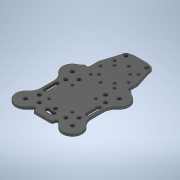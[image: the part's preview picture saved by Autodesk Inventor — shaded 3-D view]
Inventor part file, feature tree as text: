
AUTODESK INVENTOR PART (.ipt)
format: ipt  version: 2020 (Build 240168000, 168)  size: 576,000 bytes
history: native  units: in
note: dims shown in document units (in); Inventor stores cm internally (conversion verified against a paired STEP export)
features: sketch x6, projected_geometry x4, extrude x3
ambient origin geometry x8: Origin, YZ Plane, XZ Plane, XY Plane, X Axis, Y Axis, Z Axis, Center Point
bodies: Solid2 (feature_tree), Solid1 (feature_tree)
feature tree (13):
  extrude  "Extrusion1"  Depth=0.1772in
  sketch  "Sketch3"  dims[d20=0.1772in d21=0.1772in]
  sketch  "Sketch4"  dims[d22=0.1772in d23=0.1772in]
  sketch  "Sketch5"  dims[d24=0.1772in]
  extrude  "Extrusion2"  Depth=0.1772in
  extrude  "Extrusion3"  Depth=0.1772in
  sketch  "Sketch2"  dims[d18=0.1772in d19=0.1772in]
  projected_geometry  "Projected Loop2"
  projected_geometry  "Projected Loop3"
  projected_geometry  "Projected Loop4"
  projected_geometry  "Projected Loop5"
  sketch  "Sketch6"  dims[d25=0.1772in]
  sketch  "Sketch7"  dims[d26=0.1772in d27=0.1772in d28=0.1772in d29=0.1772in d30=0.1772in d31=0.1772in d32=0.1772in d33=0.3937in d34=0.0in d36=0.1772in d37=0.1772in d38=0.1772in d42=0.7092in d43=0.712in d44=0.7092in d45=0.7092in d46=0.3937in d47=0.0in d48=0.122in d49=0.122in d50=0.122in d51=0.122in d52=0.122in d53=1.0039in d54=1.0039in d55=1.0039in d56=1.0039in d57=1.4197in d58=0.3937in d59=0.0in]
